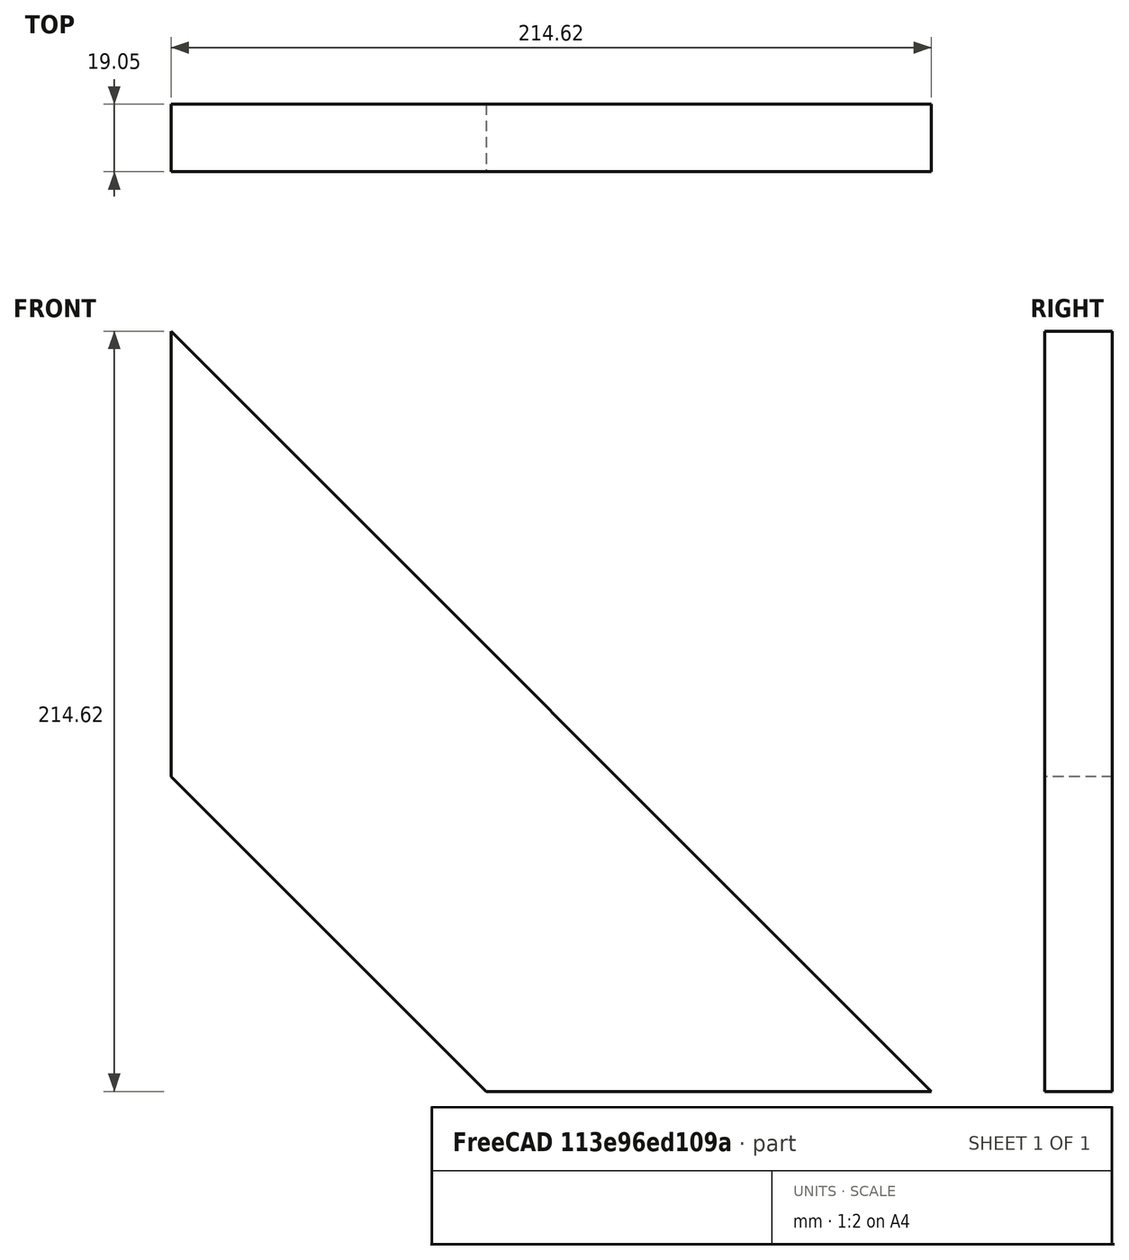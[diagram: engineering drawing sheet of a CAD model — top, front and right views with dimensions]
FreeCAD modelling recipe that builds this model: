
FCSTD DOCUMENT  (FreeCAD 0.19R24291 (Git))
Label: angle
License: All rights reserved
LicenseURL: http://en.wikipedia.org/wiki/All_rights_reserved
objects: Sketcher::SketchObject×1, PartDesign::Pad×1, PartDesign::Body×1
note: 4 computed .brp shape members not serialized (recipe doc carries the construction recipe); baked Part::Feature solids carry a one-line shape summary decoded from their .brp

FEATURE [Sketcher::SketchObject] Sketch
  FullyConstrained = true
  MapMode = 5
  Placement = pos=(0,0,0) rot=(1,0,0;1.5708rad)
  Support = -> [XZ_Plane]
  expr: Constraints[14] = 3.5 * 25.4
  expr: Constraints[9] = 3.5 * 25.4
  sketch-geometry (5):
    g0: LineSegment StartX=0 StartY=88.9 StartZ=0 EndX=88.9 EndY=0 EndZ=0
    g1: LineSegment StartX=0 StartY=214.624 StartZ=0 EndX=214.624 EndY=0 EndZ=0
    g2: LineSegment StartX=7.34 StartY=81.56 StartZ=0 EndX=70.2018 EndY=144.422 EndZ=0
    g3: LineSegment StartX=88.9 StartY=0 StartZ=0 EndX=214.624 EndY=0 EndZ=0
    g4: LineSegment StartX=0 StartY=88.9 StartZ=0 EndX=0 EndY=214.624 EndZ=0
  constraints (16):
    c: PointOnObject(g0,g-2)
    c: PointOnObject(g0,g-1)
    c: PointOnObject(g1,g-2)
    c: PointOnObject(g1,g-1)
    c: PointOnObject(g2,g0)
    c: PointOnObject(g2,g1)
    c: Angle(g0,g-1) = 0.785398
    c: Parallel(g1,g0)
    c: Perpendicular(g0,g2)
    c: Distance(g2) = 88.9
    c: Coincident(g3,g0)
    c: Coincident(g3,g1)
    c: Coincident(g4,g0)
    c: Coincident(g4,g1)
    c: DistanceX(g-1,g0) = 88.9
    c: DistanceY(g0,g2) = 81.56
FEATURE [PartDesign::Pad] Pad
  Direction = (1,1,1)
  Length = 19.05
  Length2 = 100
  Placement = pos=(0,0,0) rot=(1,0,0;1.5708rad)
  Profile = -> Sketch
  Type = 0
  expr: Length = 3 / 4 * 25.4
FEATURE [PartDesign::Body] Body
  Group = -> [Sketch,Pad]
  Origin = -> Origin
  Tip = -> Pad
